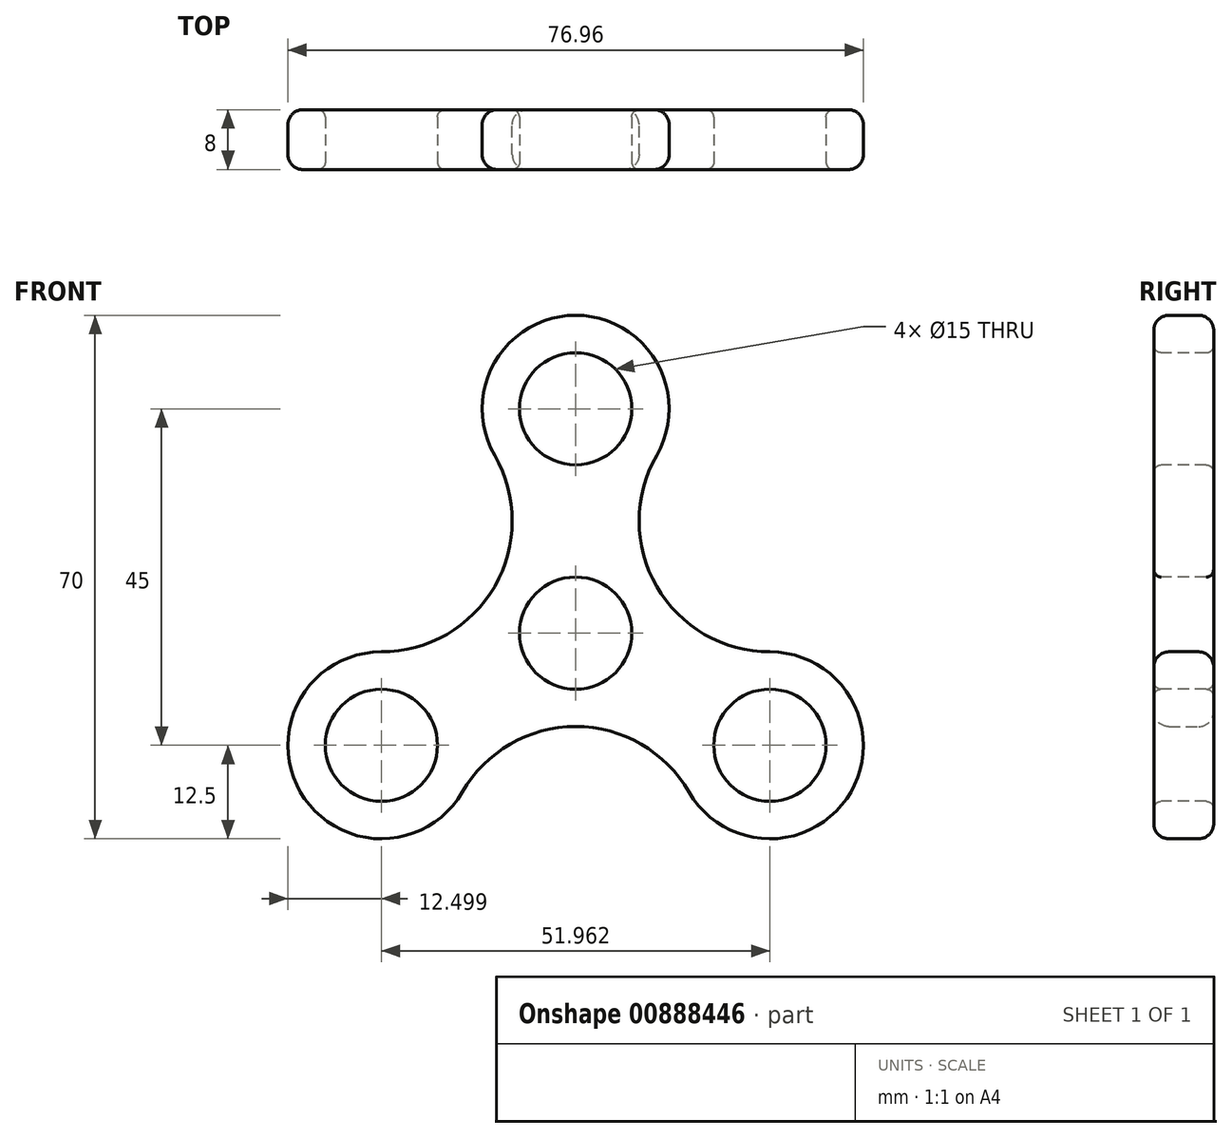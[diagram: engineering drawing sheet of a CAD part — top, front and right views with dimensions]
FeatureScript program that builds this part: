
annotation { "Feature Type Name" : "Feature", "Feature Type Description" : "" }
export const myFeature = defineFeature(function(context is Context, id is Id, definition is map)
    precondition{}
    {
        {
            var Q0;
            Q0=qCreatedBy(makeId("Front.planeOp"),FACE);
            var sketch = newSketch(context, id + "F0", { "sketchPlane" : qUnion([Q0])});
            skLineSegment(sketch, "E0", {"start": v(0, 0) * mm, "end": v(0, 30) * mm, "construction": true});
            skLineSegment(sketch, "E1.1.0", {"start": v(0, 0) * mm, "end": v(-25.98, -15) * mm, "construction": true});
            skLineSegment(sketch, "E1.2.0", {"start": v(0, 0) * mm, "end": v(25.98, -15) * mm, "construction": true});
            skPoint(sketch, "E1.center", {"position": v(0, 0) * mm});
            skArc(sketch, "E2", {"start": v(10.83, 23.75) * mm, "mid": v(0, 42.5) * mm, "end": v(-10.83, 23.75) * mm});
            skLineSegment(sketch, "E3", {"start": v(0, 0) * mm, "end": v(0, -30) * mm, "construction": true});
            skArc(sketch, "E4", {"start": v(10.83, 23.75) * mm, "mid": v(10.83, 6.25) * mm, "end": v(25.98, -2.5) * mm});
            skLineSegment(sketch, "E5.1.0", {"start": v(0, 0) * mm, "end": v(25.98, 15) * mm, "construction": true});
            skLineSegment(sketch, "E5.2.0", {"start": v(0, 0) * mm, "end": v(-25.98, 15) * mm, "construction": true});
            skArc(sketch, "E6.1.0", {"start": v(-25.98, -2.5) * mm, "mid": v(-36.8, -21.25) * mm, "end": v(-15.16, -21.25) * mm});
            skArc(sketch, "E6.2.0", {"start": v(15.16, -21.25) * mm, "mid": v(36.8, -21.25) * mm, "end": v(25.98, -2.5) * mm});
            skArc(sketch, "E7.1.0", {"start": v(-25.98, -2.5) * mm, "mid": v(-10.83, 6.25) * mm, "end": v(-10.83, 23.75) * mm});
            skArc(sketch, "E7.2.0", {"start": v(15.16, -21.25) * mm, "mid": v(0, -12.5) * mm, "end": v(-15.16, -21.25) * mm});
            skSolve(sketch);
        }
        {
            var Q0;
            Q0 = qSketchRegion(id + "F0", true);
            extrude(context, id + "F1", {"entities" : qUnion([Q0]), "endBound" : BoundingType.SYMMETRIC, "depth" : 8 * mm, "offsetDistance" : 25 * mm});
        }
        {
            var Q0;
            Q0=makeQuery(id+"F1.opExtrude","CAP_FACE",FACE,{"disambiguationData":[OSD([sQuery(id+"F0.wireOp",EDGE,"E2"),sQuery(id+"F0.wireOp",EDGE,"E4"),sQuery(id+"F0.wireOp",EDGE,"E6.1.0"),sQuery(id+"F0.wireOp",EDGE,"E6.2.0"),sQuery(id+"F0.wireOp",EDGE,"E7.1.0"),sQuery(id+"F0.wireOp",EDGE,"E7.2.0")])],"isStart":false});
            var Q1;
            Q1=makeQuery(id+"F1.opExtrude","CAP_FACE",FACE,{"disambiguationData":[OSD([sQuery(id+"F0.wireOp",EDGE,"E2"),sQuery(id+"F0.wireOp",EDGE,"E4"),sQuery(id+"F0.wireOp",EDGE,"E6.1.0"),sQuery(id+"F0.wireOp",EDGE,"E6.2.0"),sQuery(id+"F0.wireOp",EDGE,"E7.1.0"),sQuery(id+"F0.wireOp",EDGE,"E7.2.0")])],"isStart":true});
            fillet(context, id + "F2", {"entities" : qUnion([Q0, Q1]), "radius" : 2 * mm, "tangentPropagation" : true, "allowEdgeOverflow" : false});
        }
        {
            var Q0;
            Q0=makeQuery(id+"F1.opExtrude","CAP_FACE",FACE,{"disambiguationData":[OSD([sQuery(id+"F0.wireOp",EDGE,"E2"),sQuery(id+"F0.wireOp",EDGE,"E4"),sQuery(id+"F0.wireOp",EDGE,"E6.1.0"),sQuery(id+"F0.wireOp",EDGE,"E6.2.0"),sQuery(id+"F0.wireOp",EDGE,"E7.1.0"),sQuery(id+"F0.wireOp",EDGE,"E7.2.0")])],"isStart":false});
            var sketch = newSketch(context, id + "F3", { "sketchPlane" : qUnion([Q0])});
            skCircle(sketch, "E8", {"center": v(0, 0) * mm, "radius": 7.5 * mm});
            skSolve(sketch);
        }
        {
            var Q0;
            Q0 = qSketchRegion(id + "F3", true);
            extrude(context, id + "F4", {"entities" : qUnion([Q0]), "operationType" : NewBodyOperationType.REMOVE, "endBound" : BoundingType.THROUGH_ALL, "oppositeDirection" : true, "depth" : 25 * mm, "offsetDistance" : 25 * mm});
        }
        {
            var Q0;
            Q0=makeQuery(id+"F1.opExtrude","CAP_FACE",FACE,{"disambiguationData":[OSD([sQuery(id+"F0.wireOp",EDGE,"E2"),sQuery(id+"F0.wireOp",EDGE,"E4"),sQuery(id+"F0.wireOp",EDGE,"E6.1.0"),sQuery(id+"F0.wireOp",EDGE,"E6.2.0"),sQuery(id+"F0.wireOp",EDGE,"E7.1.0"),sQuery(id+"F0.wireOp",EDGE,"E7.2.0")])],"isStart":false});
            var sketch = newSketch(context, id + "F5", { "sketchPlane" : qUnion([Q0])});
            skCircle(sketch, "E9", {"center": v(0, 30) * mm, "radius": 7.5 * mm});
            skCircle(sketch, "E10.1.0", {"center": v(-25.98, -15) * mm, "radius": 7.5 * mm});
            skCircle(sketch, "E10.2.0", {"center": v(25.98, -15) * mm, "radius": 7.5 * mm});
            skPoint(sketch, "E10.center", {"position": v(0, 0) * mm});
            skSolve(sketch);
        }
        {
            var Q0;
            Q0 = qSketchRegion(id + "F5", true);
            extrude(context, id + "F6", {"entities" : qUnion([Q0]), "operationType" : NewBodyOperationType.REMOVE, "endBound" : BoundingType.THROUGH_ALL, "oppositeDirection" : true, "depth" : 25 * mm, "offsetDistance" : 25 * mm});
        }
        {
            var Q0;
            Q0=makeQuery(id+"F1.opExtrude","CAP_FACE",FACE,{"disambiguationData":[OSD([sQuery(id+"F0.wireOp",EDGE,"E2"),sQuery(id+"F0.wireOp",EDGE,"E4"),sQuery(id+"F0.wireOp",EDGE,"E6.1.0"),sQuery(id+"F0.wireOp",EDGE,"E6.2.0"),sQuery(id+"F0.wireOp",EDGE,"E7.1.0"),sQuery(id+"F0.wireOp",EDGE,"E7.2.0")])],"isStart":false});
            var Q1;
            Q1=makeQuery(id+"F1.opExtrude","CAP_FACE",FACE,{"disambiguationData":[OSD([sQuery(id+"F0.wireOp",EDGE,"E2"),sQuery(id+"F0.wireOp",EDGE,"E4"),sQuery(id+"F0.wireOp",EDGE,"E6.1.0"),sQuery(id+"F0.wireOp",EDGE,"E6.2.0"),sQuery(id+"F0.wireOp",EDGE,"E7.1.0"),sQuery(id+"F0.wireOp",EDGE,"E7.2.0")])],"isStart":true});
            fillet(context, id + "F7", {"entities" : qUnion([Q0, Q1]), "radius" : 1 * mm, "tangentPropagation" : true, "allowEdgeOverflow" : false});
        }
    });
